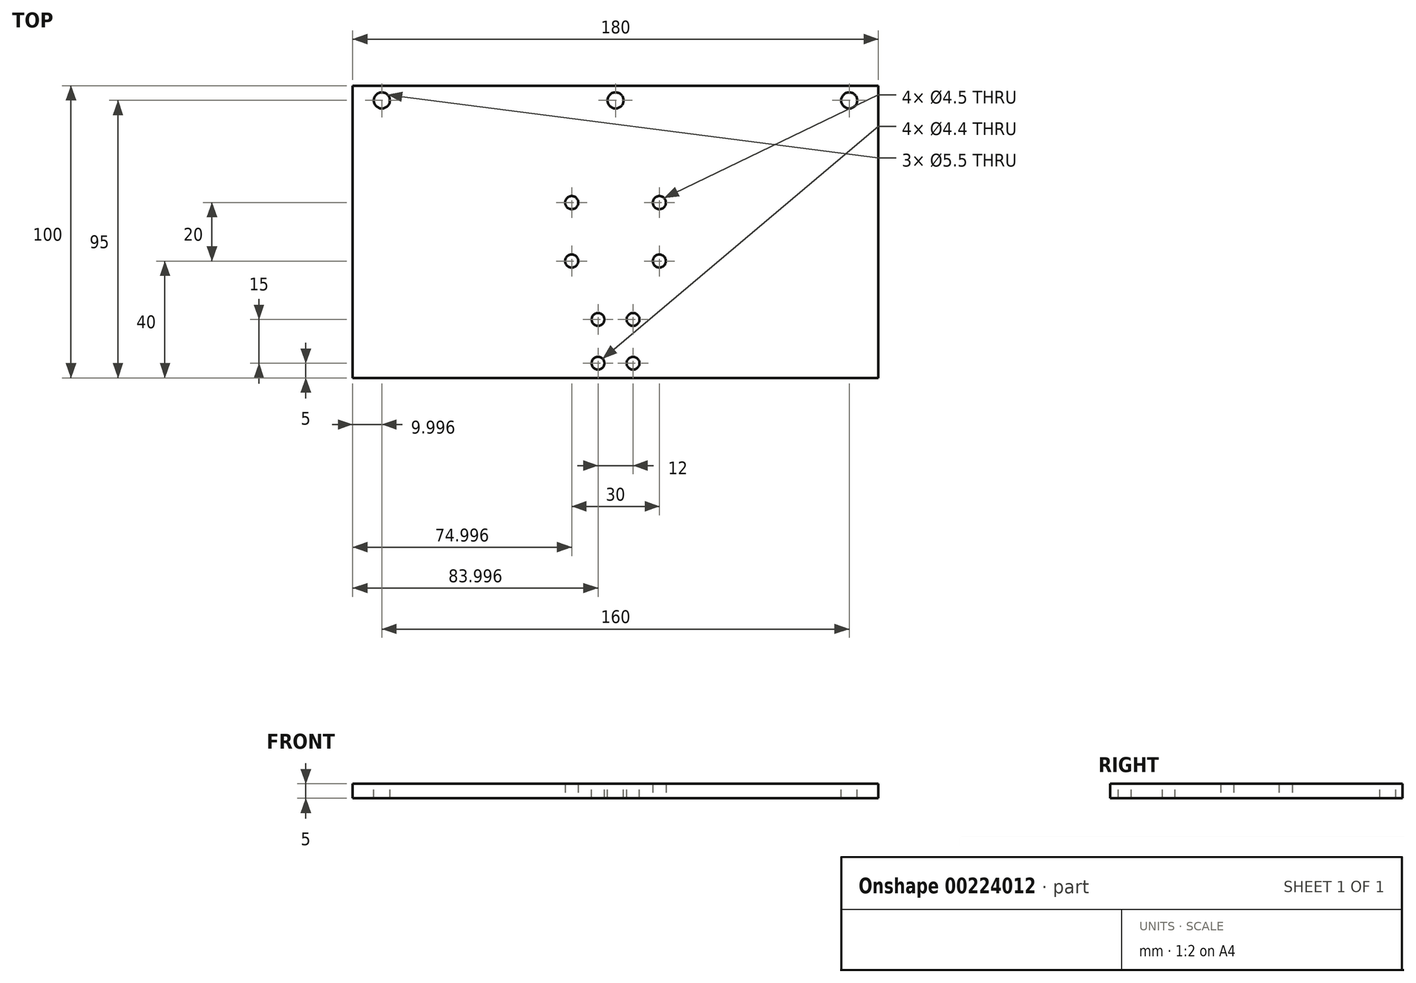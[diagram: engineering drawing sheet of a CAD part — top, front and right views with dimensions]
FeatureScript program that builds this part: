
annotation { "Feature Type Name" : "Feature", "Feature Type Description" : "" }
export const myFeature = defineFeature(function(context is Context, id is Id, definition is map)
    precondition{}
    {
        {
            var Q0;
            Q0=qCreatedBy(makeId("Top.planeOp"),FACE);
            var sketch = newSketch(context, id + "F0", { "sketchPlane" : qUnion([Q0])});
            skLineSegment(sketch, "E0.bottom", {"start": v(-50.15, 0) * mm, "end": v(129.85, 0) * mm});
            skLineSegment(sketch, "E0.top", {"start": v(-50.15, 100) * mm, "end": v(129.85, 100) * mm});
            skLineSegment(sketch, "E0.left", {"start": v(-50.15, 0) * mm, "end": v(-50.15, 100) * mm});
            skLineSegment(sketch, "E0.right", {"start": v(129.85, 0) * mm, "end": v(129.85, 100) * mm});
            skSolve(sketch);
        }
        {
            var Q0;
            Q0=makeQuery(id+"F0.imprint","IMPRINT",FACE,{"disambiguationData":[TD([[makeQuery(id+"F0.imprint","IMPRINT",EDGE,{"derivedFrom":sQuery(id+"F0.wireOp",EDGE,"E0.bottom")}),1.0]])]});
            var sketch = newSketch(context, id + "F1", { "sketchPlane" : qUnion([Q0])});
            skPoint(sketch, "E1", {"position": v(-40.15, 95) * mm});
            skPoint(sketch, "E2", {"position": v(119.85, 95) * mm});
            skPoint(sketch, "E3", {"position": v(-140.15, 95) * mm});
            skPoint(sketch, "E4", {"position": v(219.85, 95) * mm});
            skPoint(sketch, "E5", {"position": v(39.85, 95) * mm});
            skSolve(sketch);
        }
        {
            var Q0;
            Q0=makeQuery(id+"F0.imprint","IMPRINT",FACE,{"disambiguationData":[TD([[makeQuery(id+"F0.imprint","IMPRINT",EDGE,{"derivedFrom":sQuery(id+"F0.wireOp",EDGE,"E0.bottom")}),1.0]])]});
            extrude(context, id + "F2", {"entities" : qUnion([Q0]), "oppositeDirection" : true, "depth" : 5 * mm});
        }
        {
            var Q0;
            Q0=sQuery(id+"F1.wireOp",VERTEX,"E3");
            var Q1;
            Q1=sQuery(id+"F1.wireOp",VERTEX,"E1");
            var Q2;
            Q2=sQuery(id+"F1.wireOp",VERTEX,"E2");
            var Q3;
            Q3=sQuery(id+"F1.wireOp",VERTEX,"E4");
            var Q4;
            Q4=sQuery(id+"F1.wireOp",VERTEX,"E5");
            var Q5;
            Q5=makeQuery(id+"F2.opExtrude","SWEPT_BODY",BODY,{"disambiguationData":[OSD([sQuery(id+"F0.wireOp",EDGE,"E0.bottom"),sQuery(id+"F0.wireOp",EDGE,"E0.top"),sQuery(id+"F0.wireOp",EDGE,"E0.left"),sQuery(id+"F0.wireOp",EDGE,"E0.right")])]});
            hole(context, id + "F3", {"style" : HoleStyle.SIMPLE, "endStyle" : HoleEndStyle.THROUGH, "holeDiameter" : 5.5 * mm, "locations" : qUnion([Q0, Q1, Q2, Q3, Q4]), "scope" : qUnion([Q5]), "isTappedThrough" : true});
        }
        {
            var Q0;
            Q0=makeQuery(id+"F2.opExtrude","CAP_FACE",FACE,{"disambiguationData":[OSD([sQuery(id+"F0.wireOp",EDGE,"E0.bottom"),sQuery(id+"F0.wireOp",EDGE,"E0.top"),sQuery(id+"F0.wireOp",EDGE,"E0.left"),sQuery(id+"F0.wireOp",EDGE,"E0.right")])],"isStart":false});
            var sketch = newSketch(context, id + "F4", { "sketchPlane" : qUnion([Q0])});
            skPoint(sketch, "E6.positionSnap0", {"position": v(39.85, 0) * mm});
            skPoint(sketch, "E7", {"position": v(24.85, -60) * mm});
            skPoint(sketch, "E8", {"position": v(54.85, -60) * mm});
            skPoint(sketch, "E9", {"position": v(54.85, -40) * mm});
            skPoint(sketch, "E10", {"position": v(24.85, -40) * mm});
            skSolve(sketch);
        }
        {
            var Q0;
            Q0=sQuery(id+"F4.wireOp",VERTEX,"E10");
            var Q1;
            Q1=sQuery(id+"F4.wireOp",VERTEX,"E9");
            var Q2;
            Q2=sQuery(id+"F4.wireOp",VERTEX,"E8");
            var Q3;
            Q3=sQuery(id+"F4.wireOp",VERTEX,"E7");
            var Q4;
            Q4=makeQuery(id+"F2.opExtrude","SWEPT_BODY",BODY,{"disambiguationData":[OSD([sQuery(id+"F0.wireOp",EDGE,"E0.bottom"),sQuery(id+"F0.wireOp",EDGE,"E0.top"),sQuery(id+"F0.wireOp",EDGE,"E0.left"),sQuery(id+"F0.wireOp",EDGE,"E0.right")])]});
            hole(context, id + "F5", {"style" : HoleStyle.SIMPLE, "endStyle" : HoleEndStyle.THROUGH, "holeDiameter" : 4.5 * mm, "locations" : qUnion([Q0, Q1, Q2, Q3]), "scope" : qUnion([Q4]), "isTappedThrough" : true});
        }
        {
            var Q0;
            Q0=makeQuery(id+"F2.opExtrude","CAP_FACE",FACE,{"disambiguationData":[OSD([sQuery(id+"F0.wireOp",EDGE,"E0.bottom"),sQuery(id+"F0.wireOp",EDGE,"E0.top"),sQuery(id+"F0.wireOp",EDGE,"E0.left"),sQuery(id+"F0.wireOp",EDGE,"E0.right")])],"isStart":true});
            var sketch = newSketch(context, id + "F6", { "sketchPlane" : qUnion([Q0])});
            skPoint(sketch, "E11", {"position": v(33.85, 20) * mm});
            skPoint(sketch, "E12", {"position": v(33.85, 5) * mm});
            skPoint(sketch, "E13", {"position": v(45.85, 5) * mm});
            skPoint(sketch, "E14", {"position": v(45.85, 20) * mm});
            skSolve(sketch);
        }
        {
            var Q0;
            Q0=sQuery(id+"F6.wireOp",VERTEX,"E11");
            var Q1;
            Q1=sQuery(id+"F6.wireOp",VERTEX,"E14");
            var Q2;
            Q2=sQuery(id+"F6.wireOp",VERTEX,"E13");
            var Q3;
            Q3=sQuery(id+"F6.wireOp",VERTEX,"E12");
            var Q4;
            Q4=makeQuery(id+"F2.opExtrude","SWEPT_BODY",BODY,{"disambiguationData":[OSD([sQuery(id+"F0.wireOp",EDGE,"E0.bottom"),sQuery(id+"F0.wireOp",EDGE,"E0.top"),sQuery(id+"F0.wireOp",EDGE,"E0.left"),sQuery(id+"F0.wireOp",EDGE,"E0.right")])]});
            hole(context, id + "F7", {"style" : HoleStyle.SIMPLE, "endStyle" : HoleEndStyle.BLIND, "standardTappedOrClearance" : lookupTablePath({ "standard" : "ISO", "fit" : "Normal", "size" : "M4", "type" : "Clearance" }), "standardBlindInLast" : lookupTablePath({ "fit" : "Standard", "standard" : "ISO", "size" : "M4", "type" : "Clearance" }), "holeDiameter" : 4.4 * mm, "holeDepth" : 12 * mm, "locations" : qUnion([Q0, Q1, Q2, Q3]), "scope" : qUnion([Q4])});
        }
    });
